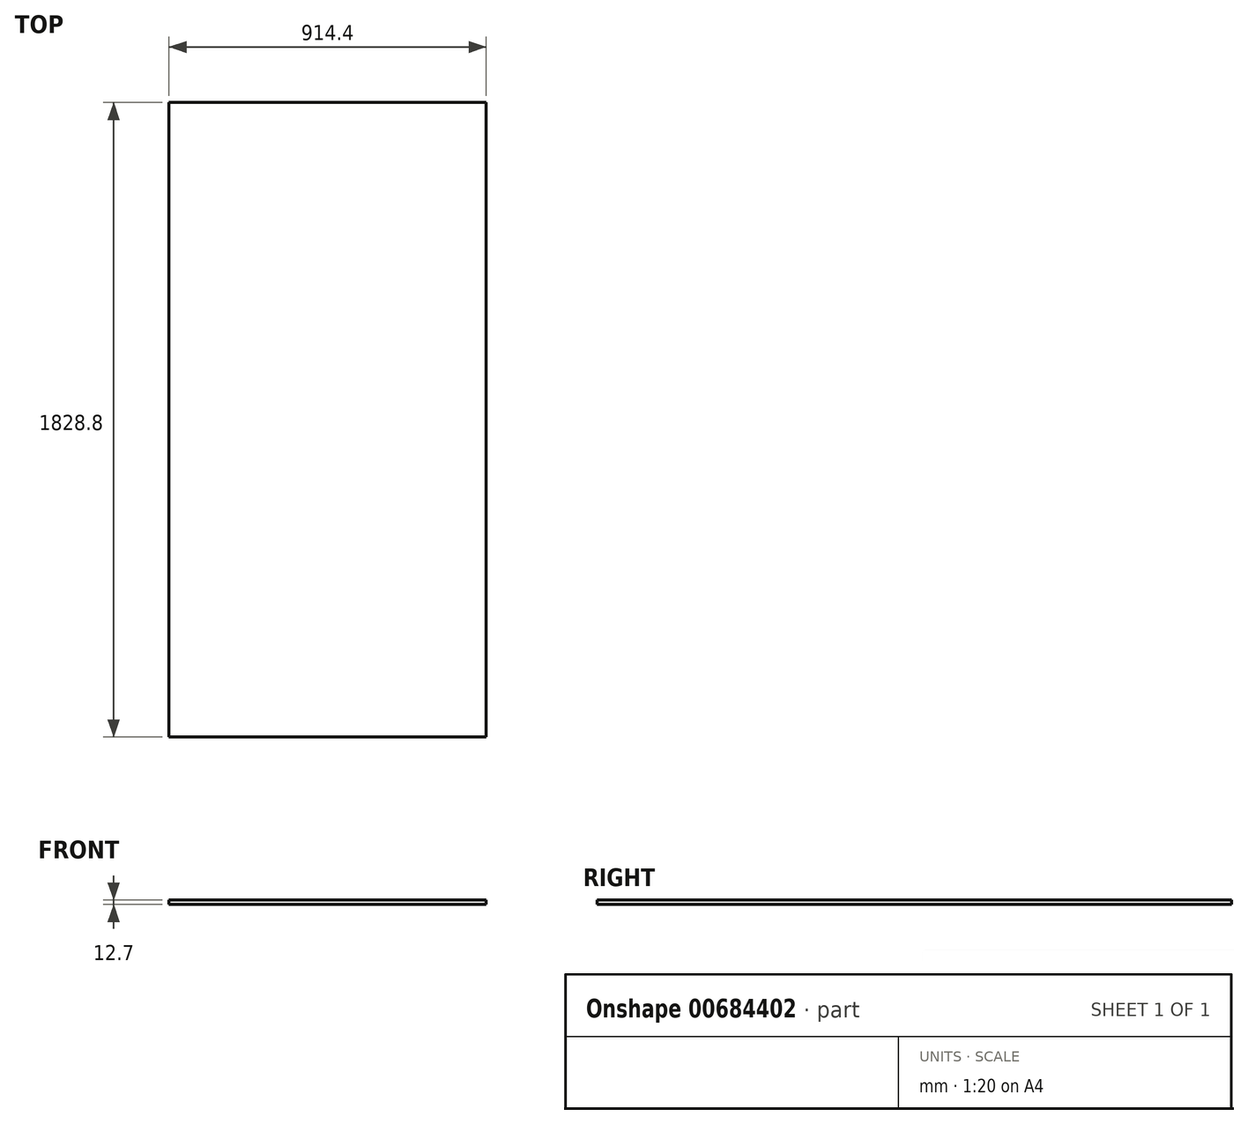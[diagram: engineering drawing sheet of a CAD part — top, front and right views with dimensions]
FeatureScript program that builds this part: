
annotation { "Feature Type Name" : "Feature", "Feature Type Description" : "" }
export const myFeature = defineFeature(function(context is Context, id is Id, definition is map)
    precondition{}
    {
        {
            var Q0;
            Q0=qCreatedBy(makeId("Top.planeOp"),FACE);
            var sketch = newSketch(context, id + "F0", { "sketchPlane" : qUnion([Q0])});
            skLineSegment(sketch, "E0.bottom", {"start": v(0, 0) * mm, "end": v(914.4, 0) * mm});
            skLineSegment(sketch, "E0.top", {"start": v(0, -1828.8) * mm, "end": v(914.4, -1828.8) * mm});
            skLineSegment(sketch, "E0.left", {"start": v(0, 0) * mm, "end": v(0, -1828.8) * mm});
            skLineSegment(sketch, "E0.right", {"start": v(914.4, 0) * mm, "end": v(914.4, -1828.8) * mm});
            skSolve(sketch);
        }
        {
            var Q0;
            Q0=makeQuery(id+"F0.imprint","IMPRINT",FACE,{"disambiguationData":[TD([[makeQuery(id+"F0.imprint","IMPRINT",EDGE,{"derivedFrom":sQuery(id+"F0.wireOp",EDGE,"E0.bottom")}),-1.0]])]});
            extrude(context, id + "F1", {"entities" : qUnion([Q0]), "depth" : 12.7 * mm, "offsetDistance" : 25.4 * mm});
        }
    });
